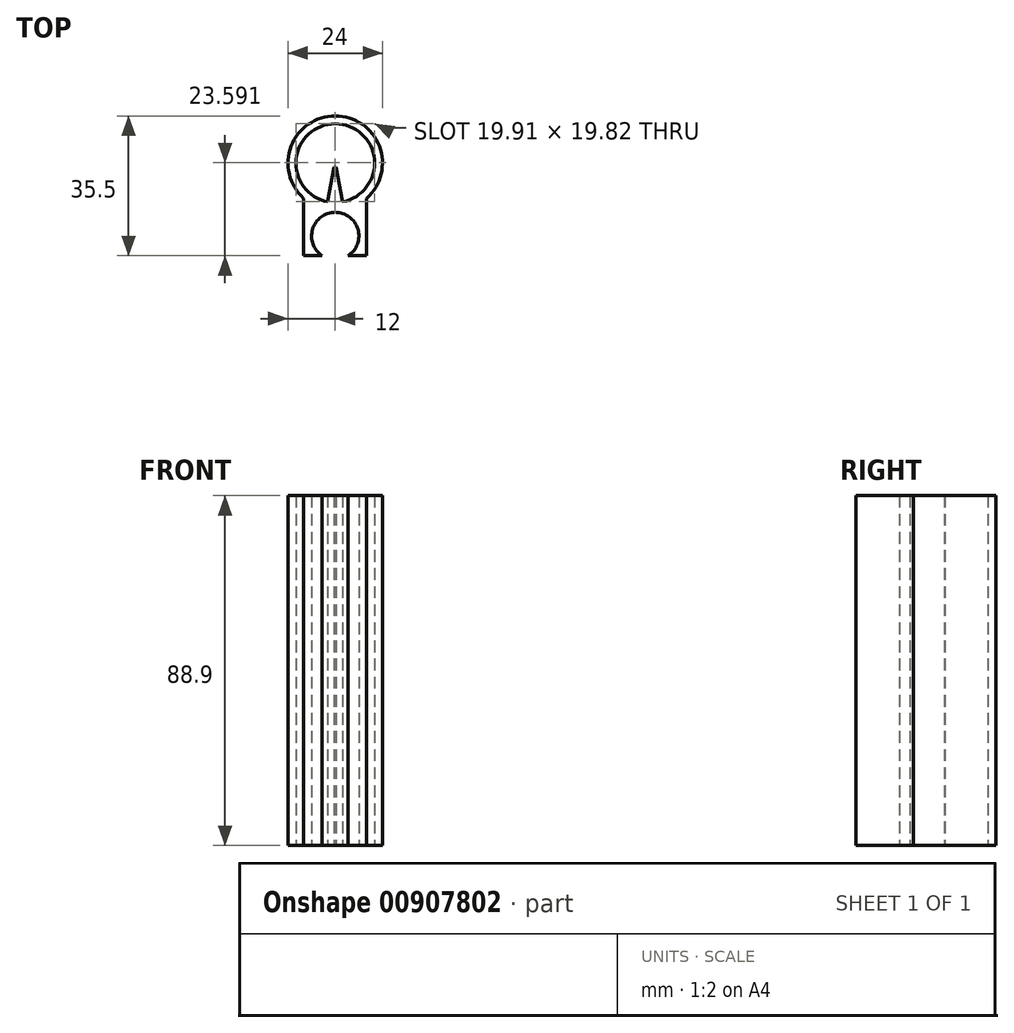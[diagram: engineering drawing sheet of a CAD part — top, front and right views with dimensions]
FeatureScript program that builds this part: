
annotation { "Feature Type Name" : "Feature", "Feature Type Description" : "" }
export const myFeature = defineFeature(function(context is Context, id is Id, definition is map)
    precondition{}
    {
        {
            var Q0;
            Q0=qCreatedBy(makeId("Top.planeOp"),FACE);
            var sketch = newSketch(context, id + "F0", { "sketchPlane" : qUnion([Q0])});
            skArc(sketch, "E0", {"start": v(8, -8.94) * mm, "mid": v(0, 12) * mm, "end": v(-8, -8.94) * mm});
            skLineSegment(sketch, "E1.bottom", {"start": v(-8, -23.5) * mm, "end": v(-3.3, -23.5) * mm});
            skLineSegment(sketch, "E1.left", {"start": v(-8, -23.5) * mm, "end": v(-8, -8.94) * mm});
            skLineSegment(sketch, "E1.right", {"start": v(8, -23.5) * mm, "end": v(8, -8.94) * mm});
            skPoint(sketch, "E1.middle", {"position": v(0, -12) * mm});
            skArc(sketch, "E2", {"start": v(3.3, -23.5) * mm, "mid": v(0, -12.48) * mm, "end": v(-3.3, -23.5) * mm});
            skPoint(sketch, "E1.top.start.orphan", {"position": v(-8, -0.5) * mm});
            skPoint(sketch, "E3.orphan", {"position": v(8, -0.5) * mm});
            skPoint(sketch, "E4.trimOffspring.end.orphan", {"position": v(0, -23.5) * mm});
            skLineSegment(sketch, "E5.trimOffspring", {"start": v(3.3, -23.5) * mm, "end": v(8, -23.5) * mm});
            skCircle(sketch, "E6", {"center": v(0, 0) * mm, "radius": 10 * mm});
            skSolve(sketch);
        }
        {
            var Q0;
            Q0 = qSketchRegion(id + "F0", true);
            extrude(context, id + "F1", {"entities" : qUnion([Q0]), "depth" : 88.9 * mm, "offsetDistance" : 25.4 * mm});
        }
        {
            var Q0;
            Q0=qCreatedBy(makeId("Top.planeOp"),FACE);
            var sketch = newSketch(context, id + "F2", { "sketchPlane" : qUnion([Q0])});
            skArc(sketch, "E7", {"start": v(-0.24, -0.97) * mm, "mid": v(0, -1) * mm, "end": v(0.24, -0.97) * mm});
            skLineSegment(sketch, "E8", {"start": v(0, -10.36) * mm, "end": v(2, -10.36) * mm});
            skLineSegment(sketch, "E9", {"start": v(2, -10.36) * mm, "end": v(-2, -10.36) * mm});
            skLineSegment(sketch, "E10", {"start": v(-2, -10.36) * mm, "end": v(-0.24, -0.97) * mm});
            skLineSegment(sketch, "E11", {"start": v(0.24, -0.97) * mm, "end": v(2, -10.36) * mm});
            skSolve(sketch);
        }
        {
            var Q0;
            Q0 = qSketchRegion(id + "F2", true);
            var Q1;
            Q1=makeQuery(id+"F1.opExtrude","CAP_FACE",FACE,{"disambiguationData":[OSD([sQuery(id+"F0.wireOp",EDGE,"E0"),sQuery(id+"F0.wireOp",EDGE,"E1.bottom"),sQuery(id+"F0.wireOp",EDGE,"E1.left"),sQuery(id+"F0.wireOp",EDGE,"E1.right"),sQuery(id+"F0.wireOp",EDGE,"E2"),sQuery(id+"F0.wireOp",EDGE,"E5.trimOffspring"),sQuery(id+"F0.wireOp",EDGE,"E6")])],"isStart":false});
            extrude(context, id + "F3", {"entities" : qUnion([Q0]), "operationType" : NewBodyOperationType.ADD, "endBound" : BoundingType.UP_TO_SURFACE, "depth" : 12.7 * mm, "endBoundEntityFace" : qUnion([Q1]), "offsetDistance" : 25.4 * mm});
        }
    });
